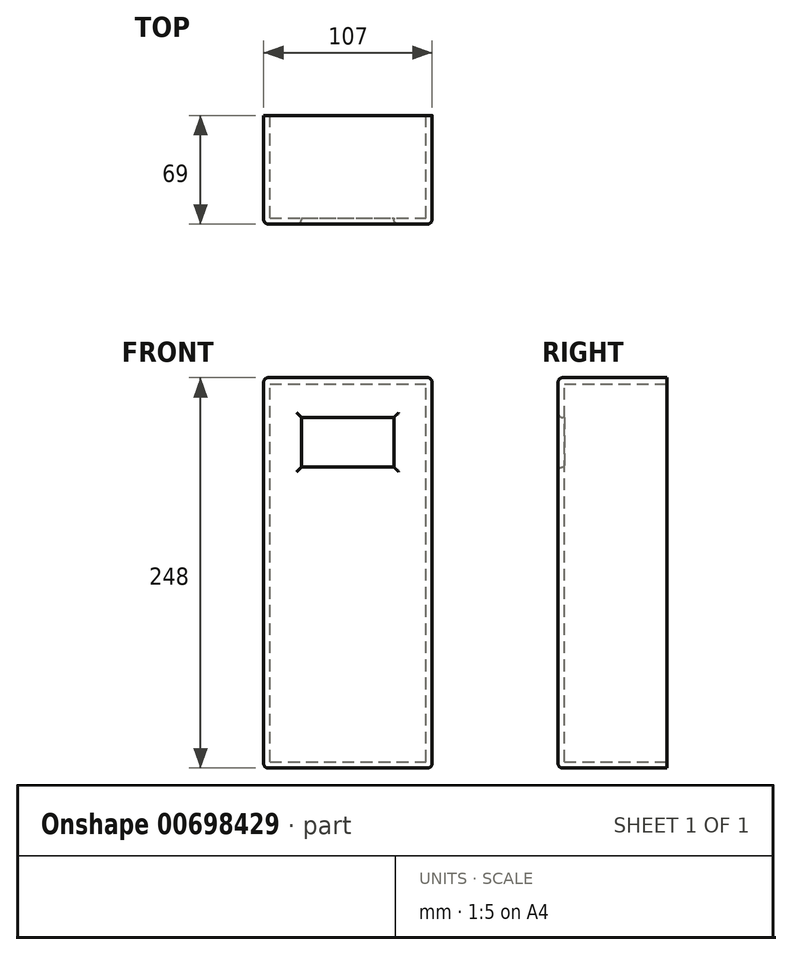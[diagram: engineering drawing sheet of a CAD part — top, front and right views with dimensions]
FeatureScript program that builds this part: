
annotation { "Feature Type Name" : "Feature", "Feature Type Description" : "" }
export const myFeature = defineFeature(function(context is Context, id is Id, definition is map)
    precondition{}
    {
        {
            var Q0;
            Q0=qCreatedBy(makeId("Front.planeOp"),FACE);
            var sketch = newSketch(context, id + "F0", { "sketchPlane" : qUnion([Q0])});
            skLineSegment(sketch, "E0.bottom", {"start": v(0, 0) * mm, "end": v(99, 0) * mm});
            skLineSegment(sketch, "E0.top", {"start": v(0, 240) * mm, "end": v(99, 240) * mm});
            skLineSegment(sketch, "E0.left", {"start": v(0, 0) * mm, "end": v(0, 240) * mm});
            skLineSegment(sketch, "E0.right", {"start": v(99, 0) * mm, "end": v(99, 240) * mm});
            skLineSegment(sketch, "E1.0", {"start": v(-4, 244) * mm, "end": v(103, 244) * mm});
            skLineSegment(sketch, "E1.1", {"start": v(-4, -4) * mm, "end": v(-4, 244) * mm});
            skLineSegment(sketch, "E1.2", {"start": v(-4, -4) * mm, "end": v(103, -4) * mm});
            skLineSegment(sketch, "E1.3", {"start": v(103, -4) * mm, "end": v(103, 244) * mm});
            skSolve(sketch);
        }
        {
            var Q0;
            Q0=makeQuery(id+"F0.imprint","IMPRINT",FACE,{"disambiguationData":[TD([[makeQuery(id+"F0.imprint","IMPRINT",EDGE,{"derivedFrom":sQuery(id+"F0.wireOp",EDGE,"E0.bottom")}),-1.0]])]});
            extrude(context, id + "F1", {"entities" : qUnion([Q0]), "depth" : 65 * mm, "offsetDistance" : 25 * mm});
        }
        {
            var Q0;
            Q0=makeQuery(id+"F1.opExtrude","CAP_FACE",FACE,{"disambiguationData":[OSD([sQuery(id+"F0.wireOp",EDGE,"E0.bottom"),sQuery(id+"F0.wireOp",EDGE,"E0.top"),sQuery(id+"F0.wireOp",EDGE,"E0.left"),sQuery(id+"F0.wireOp",EDGE,"E0.right"),sQuery(id+"F0.wireOp",EDGE,"E1.0"),sQuery(id+"F0.wireOp",EDGE,"E1.1"),sQuery(id+"F0.wireOp",EDGE,"E1.2"),sQuery(id+"F0.wireOp",EDGE,"E1.3")])],"isStart":false});
            var sketch = newSketch(context, id + "F2", { "sketchPlane" : qUnion([Q0])});
            skLineSegment(sketch, "E2.bottom", {"start": v(-4, 244) * mm, "end": v(103, 244) * mm});
            skLineSegment(sketch, "E2.top", {"start": v(-4, -4) * mm, "end": v(103, -4) * mm});
            skLineSegment(sketch, "E2.left", {"start": v(-4, 244) * mm, "end": v(-4, -4) * mm});
            skLineSegment(sketch, "E2.right", {"start": v(103, 244) * mm, "end": v(103, -4) * mm});
            skSolve(sketch);
        }
        {
            var Q0;
            Q0=makeQuery(id+"F2.imprint","IMPRINT",FACE,{"disambiguationData":[TD([[makeQuery(id+"F2.imprint","IMPRINT",EDGE,{"derivedFrom":makeQuery(id+"F1.opExtrude","CAP_EDGE",EDGE,{"disambiguationData":[OSD([sQuery(id+"F0.wireOp",EDGE,"E0.bottom")])],"isStart":false})}),1.0]])]});
            var Q1;
            Q1=makeQuery(id+"F2.imprint","IMPRINT",FACE,{"disambiguationData":[TD([[makeQuery(id+"F2.imprint","IMPRINT",EDGE,{"derivedFrom":sQuery(id+"F2.wireOp",EDGE,"E2.bottom")}),-1.0]])]});
            extrude(context, id + "F3", {"entities" : qUnion([Q0, Q1]), "operationType" : NewBodyOperationType.ADD, "depth" : 4 * mm, "offsetDistance" : 25 * mm});
        }
        {
            var Q0;
            Q0=makeQuery(id+"F3.opExtrude","CAP_FACE",FACE,{"disambiguationData":[OSD([sQuery(id+"F2.wireOp",EDGE,"E2.bottom"),sQuery(id+"F2.wireOp",EDGE,"E2.top"),sQuery(id+"F2.wireOp",EDGE,"E2.left"),sQuery(id+"F2.wireOp",EDGE,"E2.right")])],"isStart":false});
            var sketch = newSketch(context, id + "F4", { "sketchPlane" : qUnion([Q0])});
            skLineSegment(sketch, "E3.bottom", {"start": v(20, 218.7) * mm, "end": v(78.7, 218.7) * mm});
            skLineSegment(sketch, "E3.top", {"start": v(20, 187.2) * mm, "end": v(78.7, 187.2) * mm});
            skLineSegment(sketch, "E3.left", {"start": v(20, 218.7) * mm, "end": v(20, 187.2) * mm});
            skLineSegment(sketch, "E3.right", {"start": v(78.7, 218.7) * mm, "end": v(78.7, 187.2) * mm});
            skSolve(sketch);
        }
        {
            var Q0;
            Q0=makeQuery(id+"F4.imprint","IMPRINT",FACE,{"disambiguationData":[TD([[makeQuery(id+"F4.imprint","IMPRINT",EDGE,{"derivedFrom":sQuery(id+"F4.wireOp",EDGE,"E3.bottom")}),-1.0]])]});
            extrude(context, id + "F5", {"entities" : qUnion([Q0]), "operationType" : NewBodyOperationType.REMOVE, "oppositeDirection" : true, "depth" : 25 * mm, "offsetDistance" : 25 * mm});
        }
        {
            var Q0;
            Q0=makeQuery(id+"F3.boolean.opBoolean","MERGE",EDGE,{"derivedFrom":[makeQuery(id+"F1.opExtrude","SWEPT_EDGE",EDGE,{"disambiguationData":[OSD([sQuery(id+"F0.wireOp",EDGE,"E1.0"),sQuery(id+"F0.wireOp",EDGE,"E1.1")])]}),makeQuery(id+"F3.opExtrude","SWEPT_EDGE",EDGE,{"disambiguationData":[OSD([sQuery(id+"F2.wireOp",EDGE,"E2.bottom"),sQuery(id+"F2.wireOp",EDGE,"E2.left")])]})]});
            var Q1;
            Q1=makeQuery(id+"F3.boolean.opBoolean","MERGE",EDGE,{"derivedFrom":[makeQuery(id+"F1.opExtrude","SWEPT_EDGE",EDGE,{"disambiguationData":[OSD([sQuery(id+"F0.wireOp",EDGE,"E1.0"),sQuery(id+"F0.wireOp",EDGE,"E1.3")])]}),makeQuery(id+"F3.opExtrude","SWEPT_EDGE",EDGE,{"disambiguationData":[OSD([sQuery(id+"F2.wireOp",EDGE,"E2.bottom"),sQuery(id+"F2.wireOp",EDGE,"E2.right")])]})]});
            var Q2;
            Q2=makeQuery(id+"F3.boolean.opBoolean","MERGE",EDGE,{"derivedFrom":[makeQuery(id+"F1.opExtrude","SWEPT_EDGE",EDGE,{"disambiguationData":[OSD([sQuery(id+"F0.wireOp",EDGE,"E1.1"),sQuery(id+"F0.wireOp",EDGE,"E1.2")])]}),makeQuery(id+"F3.opExtrude","SWEPT_EDGE",EDGE,{"disambiguationData":[OSD([sQuery(id+"F2.wireOp",EDGE,"E2.top"),sQuery(id+"F2.wireOp",EDGE,"E2.left")])]})]});
            var Q3;
            Q3=makeQuery(id+"F3.boolean.opBoolean","MERGE",EDGE,{"derivedFrom":[makeQuery(id+"F1.opExtrude","SWEPT_EDGE",EDGE,{"disambiguationData":[OSD([sQuery(id+"F0.wireOp",EDGE,"E1.2"),sQuery(id+"F0.wireOp",EDGE,"E1.3")])]}),makeQuery(id+"F3.opExtrude","SWEPT_EDGE",EDGE,{"disambiguationData":[OSD([sQuery(id+"F2.wireOp",EDGE,"E2.top"),sQuery(id+"F2.wireOp",EDGE,"E2.right")])]})]});
            var Q4;
            Q4=makeQuery(id+"F3.opExtrude","CAP_FACE",FACE,{"disambiguationData":[OSD([sQuery(id+"F2.wireOp",EDGE,"E2.bottom"),sQuery(id+"F2.wireOp",EDGE,"E2.top"),sQuery(id+"F2.wireOp",EDGE,"E2.left"),sQuery(id+"F2.wireOp",EDGE,"E2.right")])],"isStart":false});
            fillet(context, id + "F6", {"entities" : qUnion([Q0, Q1, Q2, Q3, Q4]), "radius" : 3 * mm, "tangentPropagation" : true, "allowEdgeOverflow" : false});
        }
    });
